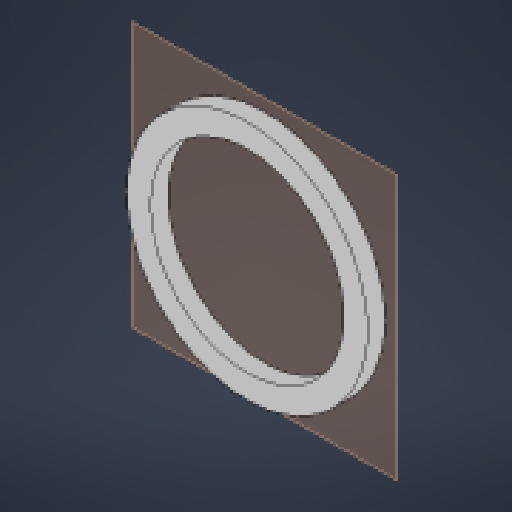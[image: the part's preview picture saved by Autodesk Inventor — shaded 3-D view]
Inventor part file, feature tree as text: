
AUTODESK INVENTOR PART (.ipt)
format: ipt  version: 2024 (Build 280153000, 153)  size: 164,864 bytes
history: native  units: in
note: dims shown in document units (in); Inventor stores cm internally (conversion verified against a paired STEP export)
features: other x4, extrude x2, plane x1, sketch x1, reference x1
ambient origin geometry x8: Origin, YZ Plane, XZ Plane, XY Plane, X Axis, Y Axis, Z Axis, Center Point
bodies: Solid1 (feature_tree)
feature tree (9):
  plane  "Work Plane1"
  sketch  "Sketch1"  dims[d0=0.35in d1=0.0in d2=0.2756in d3=1.5748in d5=360.0deg d7=0.25in d8=0.0in d10=1.5748in d11=45.0deg d12=0.409in d13=2.185in d14=1.5748in d16=360.0deg]
  extrude  "Extrusion1"  Depth=0.2756in
  extrude  "Extrusion2"  Depth=2.185in TaperAngle=360.0deg
  reference  "Reference1"
  other  "<userpath>\CodingProjects\C-AAM\CAD\V1\Base.iam"
  other  "Base.iam"
  other  "LazySusan:1"
  other  "IR:1"
